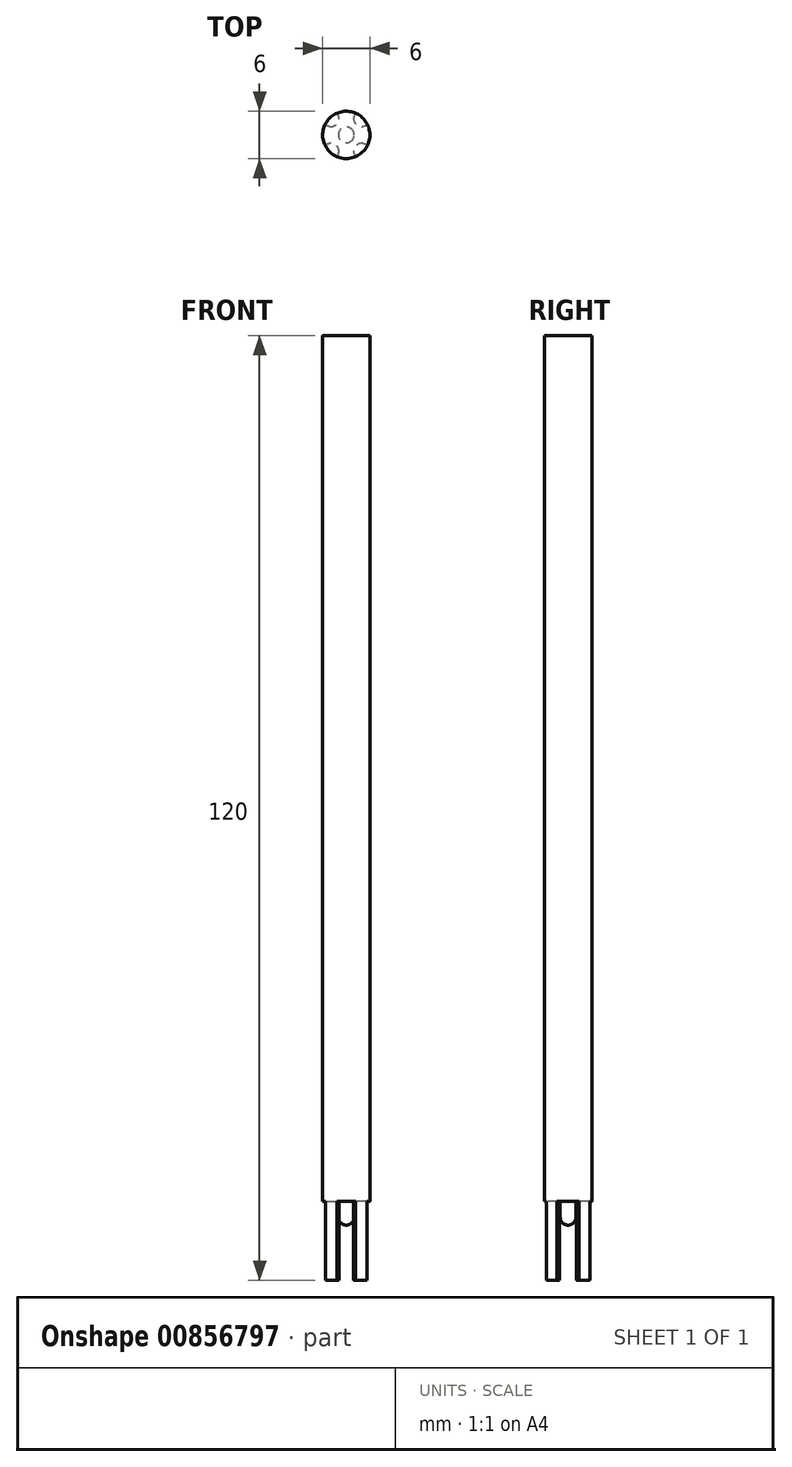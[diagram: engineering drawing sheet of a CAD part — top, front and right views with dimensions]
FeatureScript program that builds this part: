
annotation { "Feature Type Name" : "Feature", "Feature Type Description" : "" }
export const myFeature = defineFeature(function(context is Context, id is Id, definition is map)
    precondition{}
    {
        {
            var Q0;
            Q0=qCreatedBy(makeId("Top.planeOp"),FACE);
            var sketch = newSketch(context, id + "F0", { "sketchPlane" : qUnion([Q0])});
            skCircle(sketch, "E0", {"center": v(0, 0) * mm, "radius": 3 * mm});
            skSolve(sketch);
        }
        {
            var Q0;
            Q0=qSketchRegion(id+"F0",true);
            extrude(context, id + "F1", {"entities" : qUnion([Q0]), "depth" : 120 * mm, "offsetDistance" : 25 * mm});
        }
        {
            var Q0;
            Q0=makeQuery(id+"F1.opExtrude","CAP_FACE",FACE,{"disambiguationData":[OSD([sQuery(id+"F0.wireOp",EDGE,"E0")])],"isStart":true});
            var sketch = newSketch(context, id + "F2", { "sketchPlane" : qUnion([Q0])});
            skArc(sketch, "E1", {"start": v(-2.66, 1.38) * mm, "mid": v(-1.25, 1.34) * mm, "end": v(-1.2, 2.75) * mm});
            skArc(sketch, "E2.MirrorCS", {"start": v(2.66, 1.38) * mm, "mid": v(1.25, 1.34) * mm, "end": v(1.2, 2.75) * mm});
            skArc(sketch, "E3.MirrorCS", {"start": v(2.66, -1.38) * mm, "mid": v(1.25, -1.34) * mm, "end": v(1.2, -2.75) * mm});
            skArc(sketch, "E4.MirrorCS", {"start": v(-2.66, -1.38) * mm, "mid": v(-1.25, -1.34) * mm, "end": v(-1.2, -2.75) * mm});
            skSolve(sketch);
        }
        {
            var Q0;
            {var subQ3=sQuery(id+"F2.wireOp",EDGE,"E1");Q0=makeQuery(id+"F2.imprint","IMPRINT",FACE,{"disambiguationData":[TD([[makeQuery(id+"F2.imprint","IMPRINT",EDGE,{"derivedFrom":subQ3}),-1.0]])]});}
            extrude(context, id + "F3", {"entities" : qUnion([Q0]), "operationType" : NewBodyOperationType.REMOVE, "oppositeDirection" : true, "depth" : 10 * mm, "offsetDistance" : 25 * mm});
        }
        {
            var Q0;
            Q0=makeQuery(id+"F3.boolean.opBoolean","COPY",FACE,{"derivedFrom":makeQuery(id+"F3.opExtrude","CAP_FACE",FACE,{"disambiguationData":[OSD([sQuery(id+"F0.wireOp",EDGE,"E0"),sQuery(id+"F2.wireOp",EDGE,"E1"),sQuery(id+"F2.wireOp",EDGE,"E2.MirrorCS"),sQuery(id+"F2.wireOp",EDGE,"E3.MirrorCS"),sQuery(id+"F2.wireOp",EDGE,"E4.MirrorCS")])],"isStart":false})});
            var sketch = newSketch(context, id + "F4", { "sketchPlane" : qUnion([Q0])});
            skLineSegment(sketch, "E5.bottom", {"start": v(-1, 1) * mm, "end": v(1, 1) * mm});
            skLineSegment(sketch, "E5.top", {"start": v(-1, -1) * mm, "end": v(1, -1) * mm});
            skLineSegment(sketch, "E5.left", {"start": v(-1, 1) * mm, "end": v(-1, -1) * mm});
            skLineSegment(sketch, "E5.right", {"start": v(1, 1) * mm, "end": v(1, -1) * mm});
            skPoint(sketch, "E5.middle", {"position": v(0, 0) * mm});
            skSolve(sketch);
        }
        {
            var Q0;
            Q0=makeQuery(id+"F4.imprint","IMPRINT",FACE,{"disambiguationData":[TD([[makeQuery(id+"F4.imprint","IMPRINT",EDGE,{"derivedFrom":sQuery(id+"F4.wireOp",EDGE,"E5.bottom")}),-1.0]])]});
            extrude(context, id + "F5", {"entities" : qUnion([Q0]), "operationType" : NewBodyOperationType.ADD, "depth" : 3 * mm, "offsetDistance" : 25 * mm});
        }
        {
            var Q0;
            Q0=makeQuery(id+"F5.opExtrude","CAP_FACE",FACE,{"disambiguationData":[OSD([sQuery(id+"F4.wireOp",EDGE,"E5.bottom"),sQuery(id+"F4.wireOp",EDGE,"E5.top"),sQuery(id+"F4.wireOp",EDGE,"E5.left"),sQuery(id+"F4.wireOp",EDGE,"E5.right")])],"isStart":false});
            var Q1;
            Q1=makeQuery(id+"F5.opExtrude","SWEPT_EDGE",EDGE,{"disambiguationData":[OSD([sQuery(id+"F4.wireOp",EDGE,"E5.bottom"),sQuery(id+"F4.wireOp",EDGE,"E5.right")])]});
            var Q2;
            Q2=makeQuery(id+"F5.opExtrude","SWEPT_EDGE",EDGE,{"disambiguationData":[OSD([sQuery(id+"F4.wireOp",EDGE,"E5.top"),sQuery(id+"F4.wireOp",EDGE,"E5.right")])]});
            var Q3;
            Q3=makeQuery(id+"F5.opExtrude","SWEPT_EDGE",EDGE,{"disambiguationData":[OSD([sQuery(id+"F4.wireOp",EDGE,"E5.bottom"),sQuery(id+"F4.wireOp",EDGE,"E5.left")])]});
            var Q4;
            Q4=makeQuery(id+"F5.opExtrude","SWEPT_EDGE",EDGE,{"disambiguationData":[OSD([sQuery(id+"F4.wireOp",EDGE,"E5.top"),sQuery(id+"F4.wireOp",EDGE,"E5.left")])]});
            fillet(context, id + "F6", {"entities" : qUnion([Q0, Q1, Q2, Q3, Q4]), "tangentPropagation" : true, "radius" : 1 * mm, "defaultsChanged" : false, "vertexSettings" : [], "allowEdgeOverflow" : false});
        }
    });
